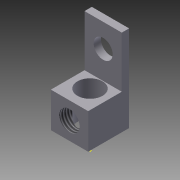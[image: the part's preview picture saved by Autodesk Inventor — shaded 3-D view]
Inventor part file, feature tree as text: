
AUTODESK INVENTOR PART (.ipt)
format: ipt  version: 2011 (Build 150239000, 239)  size: 112,640 bytes
history: native  units: mm (DEFAULTED — no unit token found)
features: other x6, sketch x4, extrude x2, hole x2, plane x2
ambient origin geometry x8: Origin, YZ Plane, XZ Plane, XY Plane, X Axis, Y Axis, Z Axis, Center Point
bodies: Solid1 (feature_tree)
feature tree (16):
  extrude  "Extrusion1"  Depth=14.0mm
  extrude  "Extrusion2"  Depth=7.0mm
  hole  "Hole1"  [1 undecoded]
  hole  "Hole2"  [1 undecoded]
  other  "Work Point1"
  other  "Work Point2"
  other  "Work Point3"
  sketch  "Sketch1"  dims[d0=12.75mm d1=14.0mm]
  sketch  "Sketch2"  dims[d2=6.375mm d3=7.0mm]
  sketch  "Sketch3"  dims[d4=12.0mm d5=0.0mm d7=2.5mm]
  sketch  "Sketch4"  dims[d8=17.5mm d9=0.0mm d10=8.0mm d11=6.375mm d12=6.5mm d13=6.0mm d14=4.0mm d15=2.0mm d16=14.3117mm d17=8.0mm d18=20.594885mm d19=6.375mm d20=6.0mm d21=6.917mm d22=6.0mm d23=4.0mm d24=2.0mm d25=14.3117mm d26=7.0mm d27=20.594885mm d28=3.175mm d29=6.35mm]
  other  "Work Axis1"
  plane  "Work Plane1"
  other  "Work Axis2"
  plane  "Work Plane2"
  other  "Work Axis3"
note: 2 required parameter values undecoded (feature->parameter linkage not recoverable at this tier; creation-order binding heuristic only, values carry confidence <= 0.55)
